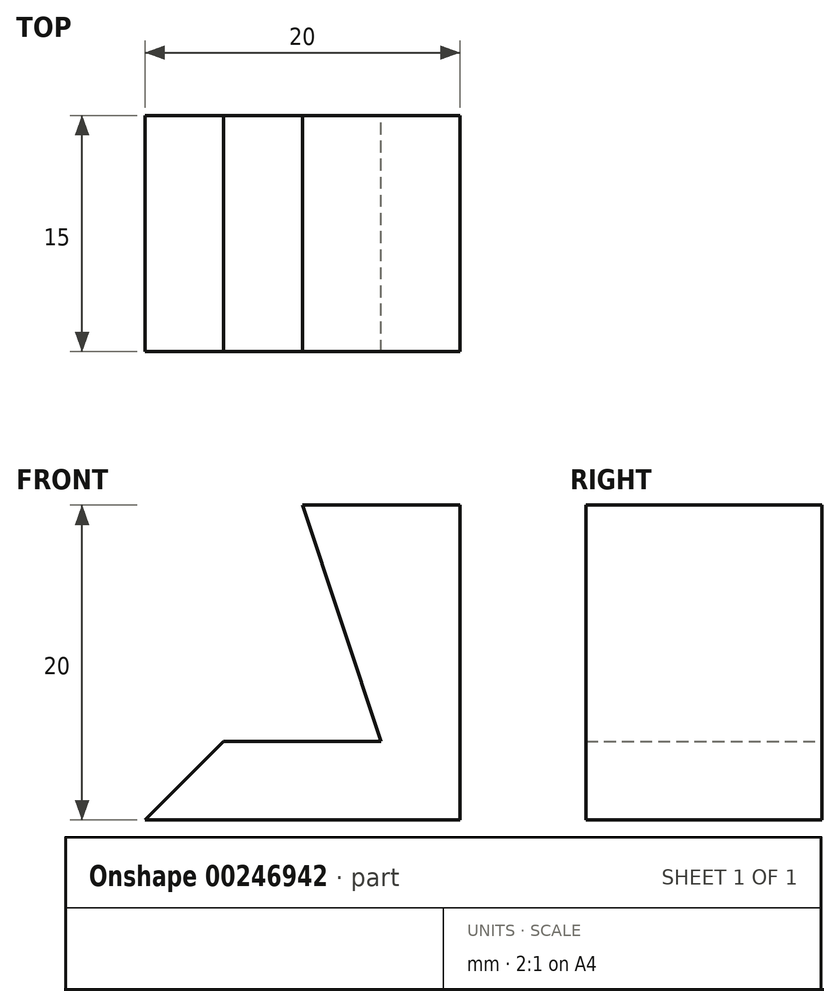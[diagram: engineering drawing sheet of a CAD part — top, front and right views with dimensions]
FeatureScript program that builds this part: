
annotation { "Feature Type Name" : "Feature", "Feature Type Description" : "" }
export const myFeature = defineFeature(function(context is Context, id is Id, definition is map)
    precondition{}
    {
        {
            var Q0;
            Q0=qCreatedBy(makeId("Front.planeOp"),FACE);
            var sketch = newSketch(context, id + "F0", { "sketchPlane" : qUnion([Q0])});
            skLineSegment(sketch, "E0", {"start": v(0, 0) * mm, "end": v(20, 0) * mm});
            skLineSegment(sketch, "E1", {"start": v(20, 0) * mm, "end": v(20, 20) * mm});
            skLineSegment(sketch, "E2", {"start": v(5, 5) * mm, "end": v(0, 0) * mm});
            skLineSegment(sketch, "E3", {"start": v(5, 5) * mm, "end": v(15, 5) * mm});
            skLineSegment(sketch, "E4", {"start": v(10, 20) * mm, "end": v(15, 5) * mm});
            skLineSegment(sketch, "E5", {"start": v(10, 20) * mm, "end": v(20, 20) * mm});
            skSolve(sketch);
        }
        {
            var Q0;
            Q0=makeQuery(id+"F0.imprint","IMPRINT",FACE,{"disambiguationData":[TD([[makeQuery(id+"F0.imprint","IMPRINT",EDGE,{"derivedFrom":sQuery(id+"F0.wireOp",EDGE,"E0")}),1.0]])]});
            extrude(context, id + "F1", {"entities" : qUnion([Q0]), "depth" : 15 * mm});
        }
    });
